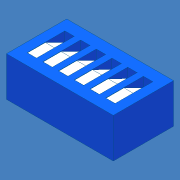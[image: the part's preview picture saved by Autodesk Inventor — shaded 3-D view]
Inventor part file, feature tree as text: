
AUTODESK INVENTOR PART (.ipt)
format: ipt  version: unknown  size: 246,272 bytes
history: native  units: mm (DEFAULTED — no unit token found)
features: extrude x4, sketch x4, pattern_linear x2
ambient origin geometry x8: Origin, YZ Plane, XZ Plane, XY Plane, X Axis, Y Axis, Z Axis, Center Point
feature tree (10):
  extrude  "Extrusion1"  Depth=17.272mm
  extrude  "Extrusion2"  Depth=1.524mm
  extrude  "Extrusion6"  Depth=1.524mm
  extrude  "Extrusion7"  Depth=0.0254mm
  pattern_linear  "Rectangular Pattern5"  Spacing1=2.5146mm  [1 undecoded]
  pattern_linear  "Rectangular Pattern6"  Spacing1=3.175mm  [1 undecoded]
  sketch  "Sketch1"  dims[d0=9.7409mm d1=17.272mm]
  sketch  "Sketch2"  dims[d2=6.3881mm d3=0.0mm d4=1.524mm]
  sketch  "Sketch6"  dims[d5=6.096mm d7=1.524mm]
  sketch  "Sketch7"  dims[d8=2.54mm d9=0.0mm d38=0.0254mm d39=2.5146mm d40=0.0mm d41=3.175mm d42=1.5875mm d43=2.54mm d44=0.0mm d45=60.0mm d47=2.54mm d48=60.0mm d50=2.54mm]
note: 2 required parameter values undecoded (feature->parameter linkage not recoverable at this tier; creation-order binding heuristic only, values carry confidence <= 0.55)
